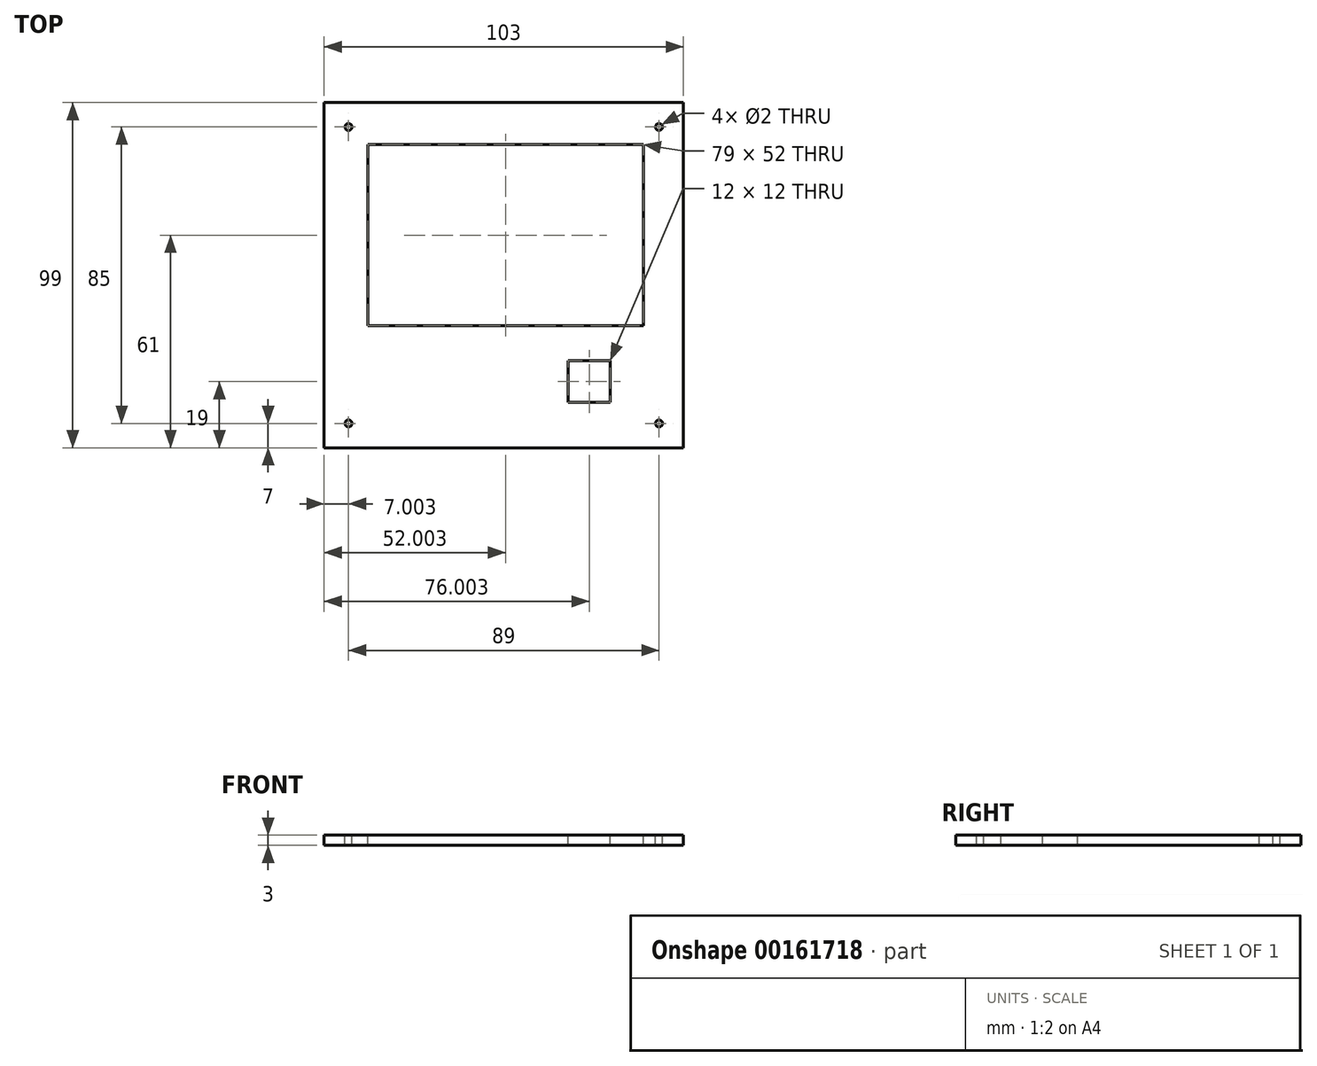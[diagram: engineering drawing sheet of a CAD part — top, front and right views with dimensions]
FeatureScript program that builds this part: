
annotation { "Feature Type Name" : "Feature", "Feature Type Description" : "" }
export const myFeature = defineFeature(function(context is Context, id is Id, definition is map)
    precondition{}
    {
        {
            var Q0;
            Q0=qCreatedBy(makeId("Top.planeOp"),FACE);
            var sketch = newSketch(context, id + "F0", { "sketchPlane" : qUnion([Q0])});
            skLineSegment(sketch, "E0.bottom", {"start": v(-49.88, 36.35) * mm, "end": v(53.12, 36.35) * mm});
            skLineSegment(sketch, "E0.top", {"start": v(-49.88, -62.65) * mm, "end": v(53.12, -62.65) * mm});
            skLineSegment(sketch, "E0.left", {"start": v(-49.88, 36.35) * mm, "end": v(-49.88, -62.65) * mm});
            skLineSegment(sketch, "E0.right", {"start": v(53.12, 36.35) * mm, "end": v(53.12, -62.65) * mm});
            skSolve(sketch);
        }
        {
            var Q0;
            Q0=makeQuery(id+"F0.imprint","IMPRINT",FACE,{"disambiguationData":[TD([[makeQuery(id+"F0.imprint","IMPRINT",EDGE,{"derivedFrom":sQuery(id+"F0.wireOp",EDGE,"E0.bottom")}),-1.0]])]});
            var sketch = newSketch(context, id + "F1", { "sketchPlane" : qUnion([Q0])});
            skLineSegment(sketch, "E1.bottom", {"start": v(-37.38, 24.35) * mm, "end": v(41.62, 24.35) * mm});
            skLineSegment(sketch, "E1.top", {"start": v(-37.38, -27.65) * mm, "end": v(41.62, -27.65) * mm});
            skLineSegment(sketch, "E1.left", {"start": v(-37.38, 24.35) * mm, "end": v(-37.38, -27.65) * mm});
            skLineSegment(sketch, "E1.right", {"start": v(41.62, 24.35) * mm, "end": v(41.62, -27.65) * mm});
            skSolve(sketch);
        }
        {
            var Q0;
            Q0=qCreatedBy(makeId("Top.planeOp"),FACE);
            var sketch = newSketch(context, id + "F2", { "sketchPlane" : qUnion([Q0])});
            skLineSegment(sketch, "E2.bottom", {"start": v(20.12, -37.65) * mm, "end": v(32.12, -37.65) * mm});
            skLineSegment(sketch, "E2.top", {"start": v(20.12, -49.65) * mm, "end": v(32.12, -49.65) * mm});
            skLineSegment(sketch, "E2.left", {"start": v(20.12, -37.65) * mm, "end": v(20.12, -49.65) * mm});
            skLineSegment(sketch, "E2.right", {"start": v(32.12, -37.65) * mm, "end": v(32.12, -49.65) * mm});
            skSolve(sketch);
        }
        {
            var Q0;
            Q0 = qSketchRegion(id + "F0", true);
            extrude(context, id + "F3", {"entities" : qUnion([Q0]), "oppositeDirection" : true, "depth" : 3 * mm});
        }
        {
            var Q0;
            Q0=makeQuery(id+"F1.imprint","IMPRINT",FACE,{"disambiguationData":[TD([[makeQuery(id+"F1.imprint","IMPRINT",EDGE,{"derivedFrom":sQuery(id+"F1.wireOp",EDGE,"E1.bottom")}),-1.0]])]});
            extrude(context, id + "F4", {"entities" : qUnion([Q0]), "operationType" : NewBodyOperationType.REMOVE, "endBound" : BoundingType.THROUGH_ALL, "oppositeDirection" : true, "depth" : 25 * mm});
        }
        {
            var Q0;
            Q0=makeQuery(id+"F2.imprint","IMPRINT",FACE,{"disambiguationData":[TD([[makeQuery(id+"F2.imprint","IMPRINT",EDGE,{"derivedFrom":sQuery(id+"F2.wireOp",EDGE,"E2.bottom")}),-1.0]])]});
            extrude(context, id + "F5", {"entities" : qUnion([Q0]), "operationType" : NewBodyOperationType.REMOVE, "endBound" : BoundingType.THROUGH_ALL, "oppositeDirection" : true, "depth" : 25 * mm});
        }
        {
            var Q0;
            Q0=makeQuery(id+"F3.opExtrude","CAP_FACE",FACE,{"disambiguationData":[OSD([sQuery(id+"F0.wireOp",EDGE,"E0.bottom"),sQuery(id+"F0.wireOp",EDGE,"E0.top"),sQuery(id+"F0.wireOp",EDGE,"E0.left"),sQuery(id+"F0.wireOp",EDGE,"E0.right")])],"isStart":true});
            var sketch = newSketch(context, id + "F6", { "sketchPlane" : qUnion([Q0])});
            skPoint(sketch, "E3.first.point", {"position": v(-1.83, 56.36) * mm});
            skPoint(sketch, "E3.second.point", {"position": v(19.8, 24.35) * mm});
            skPoint(sketch, "E3.third.point", {"position": v(0, 33.45) * mm});
            skCircle(sketch, "E4", {"center": v(-42.88, 29.35) * mm, "radius": 1 * mm});
            skCircle(sketch, "E5.1.0.0", {"center": v(-134.13, 29.35) * mm, "radius": 1 * mm});
            skLineSegment(sketch, "E5.direction1", {"start": v(-42.88, 29.35) * mm, "end": v(-134.13, 29.35) * mm, "construction": true});
            skCircle(sketch, "E6", {"center": v(46.12, 29.35) * mm, "radius": 1 * mm});
            skCircle(sketch, "E7", {"center": v(-42.88, -55.65) * mm, "radius": 1 * mm});
            skCircle(sketch, "E8", {"center": v(46.12, -55.65) * mm, "radius": 1 * mm});
            skSolve(sketch);
        }
        {
            var Q0;
            Q0 = qSketchRegion(id + "F6", true);
            extrude(context, id + "F7", {"entities" : qUnion([Q0]), "operationType" : NewBodyOperationType.REMOVE, "endBound" : BoundingType.THROUGH_ALL, "oppositeDirection" : true, "depth" : 25 * mm});
        }
    });
